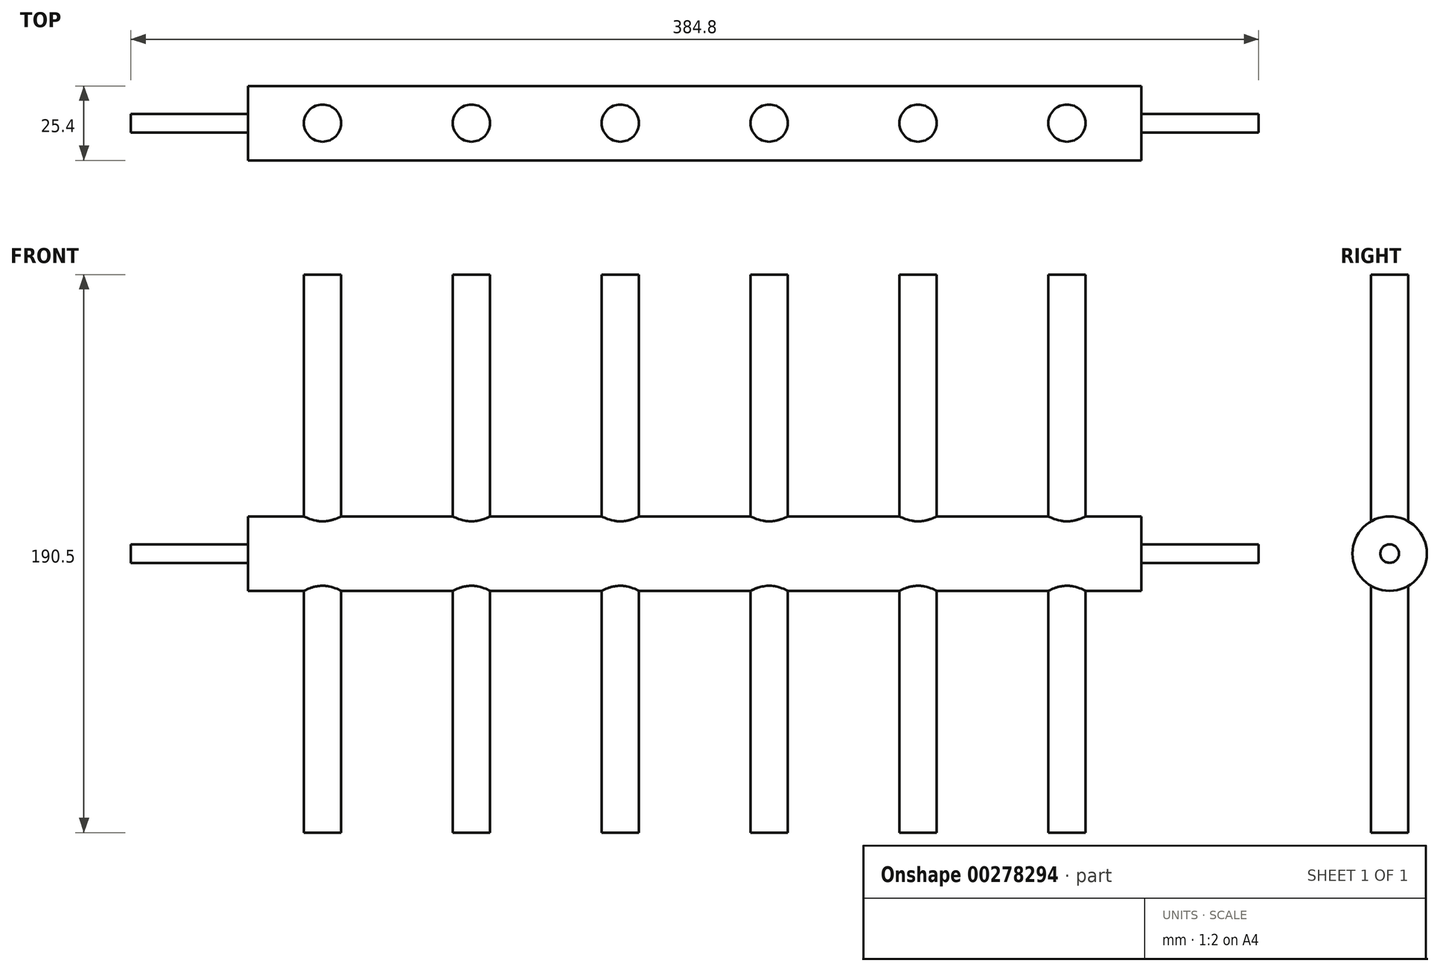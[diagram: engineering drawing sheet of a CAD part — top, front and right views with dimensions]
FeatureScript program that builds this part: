
annotation { "Feature Type Name" : "Feature", "Feature Type Description" : "" }
export const myFeature = defineFeature(function(context is Context, id is Id, definition is map)
    precondition{}
    {
        {
            var Q0;
            Q0=qCreatedBy(makeId("Right.planeOp"),FACE);
            var sketch = newSketch(context, id + "F0", { "sketchPlane" : qUnion([Q0])});
            skCircle(sketch, "E0", {"center": v(0, 0) * mm, "radius": 12.7 * mm});
            skSolve(sketch);
        }
        {
            var Q0;
            Q0 = qSketchRegion(id + "F0", true);
            extrude(context, id + "F1", {"entities" : qUnion([Q0]), "depth" : 304.8 * mm});
        }
        {
            var Q0;
            Q0=makeQuery(id+"F1.opExtrude","CAP_FACE",FACE,{"disambiguationData":[OSD([sQuery(id+"F0.wireOp",EDGE,"E0")])],"isStart":false});
            var sketch = newSketch(context, id + "F2", { "sketchPlane" : qUnion([Q0])});
            skCircle(sketch, "E1", {"center": v(0, 0) * mm, "radius": 3.18 * mm});
            skSolve(sketch);
        }
        {
            var Q0;
            Q0 = qSketchRegion(id + "F2", true);
            extrude(context, id + "F3", {"entities" : qUnion([Q0]), "operationType" : NewBodyOperationType.ADD, "depth" : 40 * mm});
        }
        {
            var Q0;
            Q0=makeQuery(id+"F1.opExtrude","CAP_FACE",FACE,{"disambiguationData":[OSD([sQuery(id+"F0.wireOp",EDGE,"E0")])],"isStart":true});
            var sketch = newSketch(context, id + "F4", { "sketchPlane" : qUnion([Q0])});
            skCircle(sketch, "E2", {"center": v(0, 0) * mm, "radius": 3.18 * mm});
            skSolve(sketch);
        }
        {
            var Q0;
            Q0 = qSketchRegion(id + "F4", true);
            extrude(context, id + "F5", {"entities" : qUnion([Q0]), "operationType" : NewBodyOperationType.ADD, "depth" : 40 * mm});
        }
        {
            var Q0;
            Q0=qCreatedBy(makeId("Top.planeOp"),FACE);
            var sketch = newSketch(context, id + "F6", { "sketchPlane" : qUnion([Q0])});
            skCircle(sketch, "E3", {"center": v(177.8, 0) * mm, "radius": 6.35 * mm});
            skLineSegment(sketch, "E4", {"start": v(177.8, 0) * mm, "end": v(127, 0) * mm});
            skLineSegment(sketch, "E5", {"start": v(127, 0) * mm, "end": v(76.2, 0) * mm});
            skLineSegment(sketch, "E6", {"start": v(76.2, 0) * mm, "end": v(25.4, 0) * mm});
            skLineSegment(sketch, "E7", {"start": v(0, 0) * mm, "end": v(25.4, 0) * mm});
            skLineSegment(sketch, "E8", {"start": v(177.8, 0) * mm, "end": v(228.6, 0) * mm});
            skLineSegment(sketch, "E9", {"start": v(228.6, 0) * mm, "end": v(279.4, 0) * mm});
            skCircle(sketch, "E10", {"center": v(25.4, 0) * mm, "radius": 6.35 * mm});
            skCircle(sketch, "E11", {"center": v(76.2, 0) * mm, "radius": 6.35 * mm});
            skCircle(sketch, "E12", {"center": v(127, 0) * mm, "radius": 6.35 * mm});
            skCircle(sketch, "E13", {"center": v(228.6, 0) * mm, "radius": 6.35 * mm});
            skCircle(sketch, "E14", {"center": v(279.4, 0) * mm, "radius": 6.35 * mm});
            skSolve(sketch);
        }
        {
            var Q0;
            Q0 = qSketchRegion(id + "F6", true);
            extrude(context, id + "F7", {"entities" : qUnion([Q0]), "operationType" : NewBodyOperationType.ADD, "depth" : 95.25 * mm, "hasSecondDirection" : true, "secondDirectionOppositeDirection" : true, "secondDirectionDepth" : 95.25 * mm});
        }
    });
